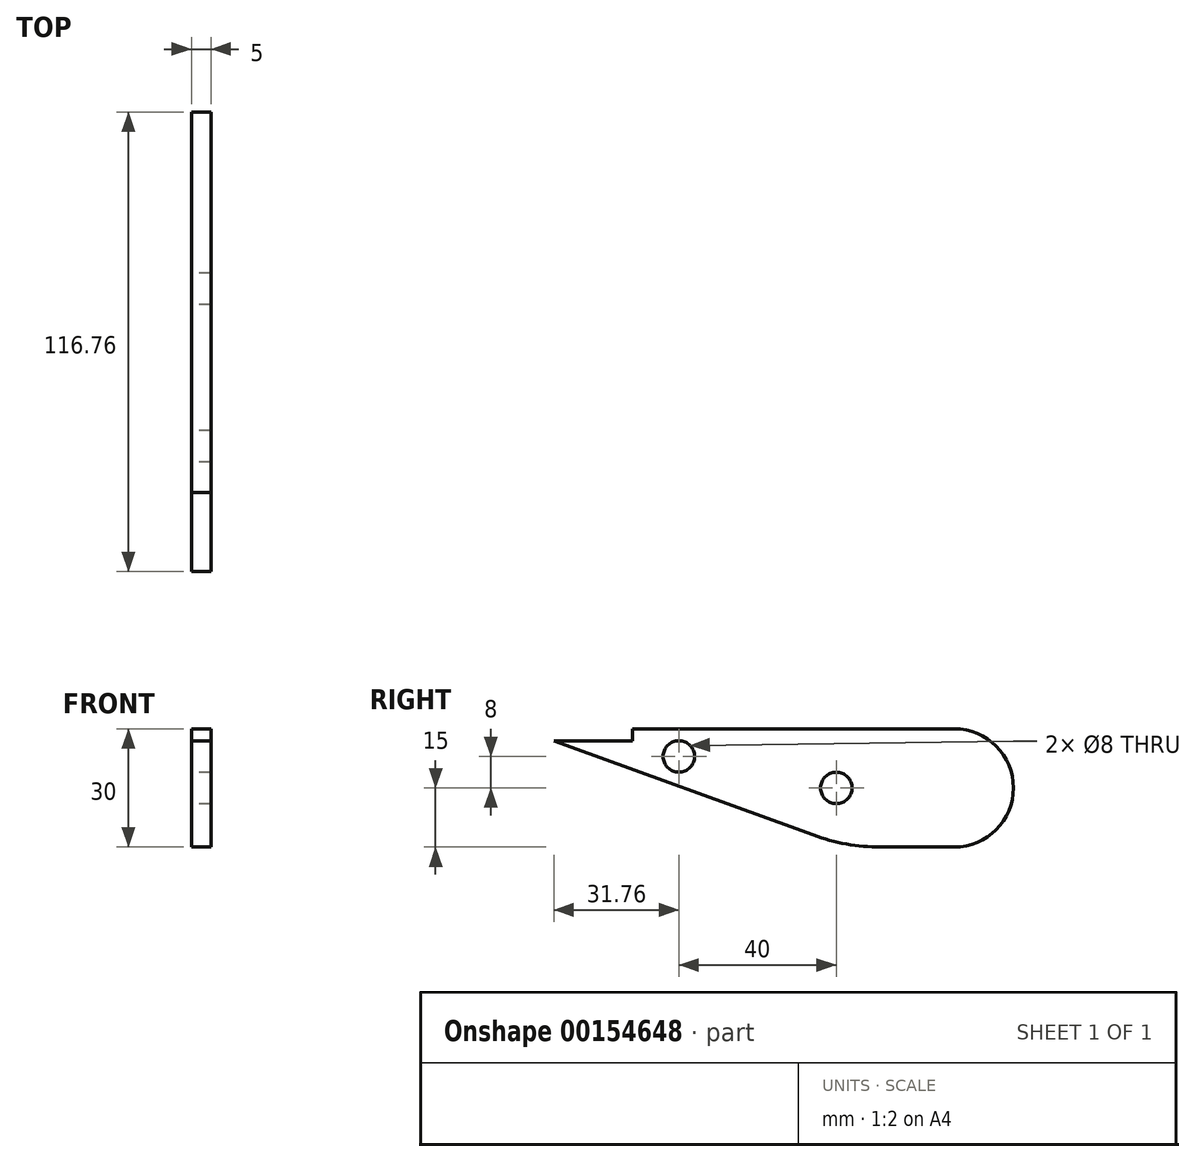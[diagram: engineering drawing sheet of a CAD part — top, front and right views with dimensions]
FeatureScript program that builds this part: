
annotation { "Feature Type Name" : "Feature", "Feature Type Description" : "" }
export const myFeature = defineFeature(function(context is Context, id is Id, definition is map)
    precondition{}
    {
        {
            var Q0;
            Q0=qCreatedBy(makeId("Right.planeOp"),FACE);
            var sketch = newSketch(context, id + "F0", { "sketchPlane" : qUnion([Q0])});
            skLineSegment(sketch, "E0.bottom", {"start": v(-31.76, 15) * mm, "end": v(50, 15) * mm});
            skLineSegment(sketch, "E0.top", {"start": v(31.24, -15) * mm, "end": v(50, -15) * mm});
            skArc(sketch, "E1", {"start": v(50, -15) * mm, "mid": v(65, 0) * mm, "end": v(50, 15) * mm});
            skLineSegment(sketch, "E2", {"start": v(-51.76, 12) * mm, "end": v(14.14, -11.98) * mm});
            skCircle(sketch, "E3", {"center": v(20, 0) * mm, "radius": 4 * mm});
            skPoint(sketch, "E4.visualSharp", {"position": v(22.42, -15) * mm});
            skArc(sketch, "E4.filletArc", {"start": v(14.14, -11.98) * mm, "mid": v(22.56, -14.24) * mm, "end": v(31.24, -15) * mm});
            skPoint(sketch, "E5.visualSharp", {"position": v(-60, 15) * mm});
            skCircle(sketch, "E6", {"center": v(-20, 8) * mm, "radius": 4 * mm});
            skLineSegment(sketch, "E7.top", {"start": v(-31.76, 12) * mm, "end": v(-51.76, 12) * mm});
            skLineSegment(sketch, "E7.left", {"start": v(-31.76, 15) * mm, "end": v(-31.76, 12) * mm});
            skSolve(sketch);
        }
        {
            var Q0;
            Q0=qSketchRegion(id+"F0",true);
            extrude(context, id + "F1", {"entities" : qUnion([Q0]), "depth" : 5 * mm});
        }
    });
